# Revit family: Adriatico entrada superior
name_source: partatom
category: Aparatos sanitarios
revit_build: Autodesk Revit 2016 (Build: 20151007_0715(x64)
units: mm (PartAtom-declared; Revit-internal decimal feet)

## family parameters
Anfitrión = Muro
Compartido = No
Corte con vacíos al cargar = No
Cota de conector redondo = Diámetro de uso
Número OmniClass = 23.45.55.11
Punto de cálculo de habitación = No
Siempre vertical = Sí
Tipo de pieza = Normal
Título OmniClass = Sanitary Components

## types (1)
- Tipo 1
    Acabado = Brillante
    Altura Nominal = 430 mm
    Ancho Nominal = 397 mm  [stored 1.30249 ft]
    Características = Taza institucional de alta eficiencia en consumo de agua y alta capacidad de evacuación de descarga, perfecta para espacios comerciales, turismo, educación y salud.
    Color = Blanco
    Comentarios de tipo = Accesorio incluido: Racor metálico de 1 1/2" para fluxómetro
    Cumplimiento de Norma = ICONTEC NTC No. 920-1 ASME A112.19.2 CSA B 45.1 EPA WATERSENSE, NOM 009 / 010
    Código de montaje = D2010100
    Descripción 1 = Taza Adriatico Al de anillo cerrado de entrada superior
    Descripción de la garantía = Garantía limitada de por vida
    Diámetro de conexión entrada = 1 1/2"
    Diámetro de conexión sanitaria = 4 "
    Fabricante = CORONA / COLCERAMICA
    Forma = Rectangular ovalada
    Imagen de tipo = <Ninguno>
    Longitud Nominal = 715 mm  [stored 2.3458 ft]
    Material = Ceramica_Corona_Blanco
    Material Secundario = Plastico_Corona_Blanco
    Material de Fabricación = Porcelana Sanitaria
    Modelo = Taza ADRIATICO AL anillo cerrado de entrada superior
    Nombre = TAZA ADRIATICO AL
    Nombre del Fabricante = CORONA / COLCERAMICA
    Número de modelo = 013181001
    Presión máxima = 80 PSI
    Presión mínima = 20 PSI
    Responsable de garantía partes = www.corona.com.co
    Tamaño = ( H x L x W ) 430 x 715 x 397
    Tipo de Activo = FIjo
    URL = https://s3.amazonaws.com

note: [stored X ft] marks values corroborated as IEEE doubles in the binary element streams (Revit-internal decimal feet)
